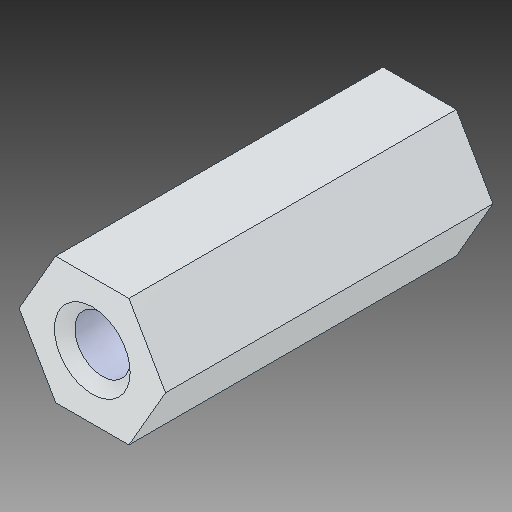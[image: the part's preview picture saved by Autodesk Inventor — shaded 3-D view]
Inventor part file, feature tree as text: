
AUTODESK INVENTOR PART (.ipt)
format: ipt  version: 2018 (Build 220112000, 112)  size: 119,808 bytes
history: native  units: in
note: dims shown in document units (in); Inventor stores cm internally (conversion verified against a paired STEP export)
features: chamfer x1
ambient origin geometry x8: Origin, YZ Plane, XZ Plane, XY Plane, X Axis, Y Axis, Z Axis, Center Point
bodies: Solid1 (feature_tree)
feature tree (1):
  chamfer  "Chamfer1"  [1 undecoded]
note: 1 required parameter value undecoded (feature->parameter linkage not recoverable at this tier; creation-order binding heuristic only, values carry confidence <= 0.55)
